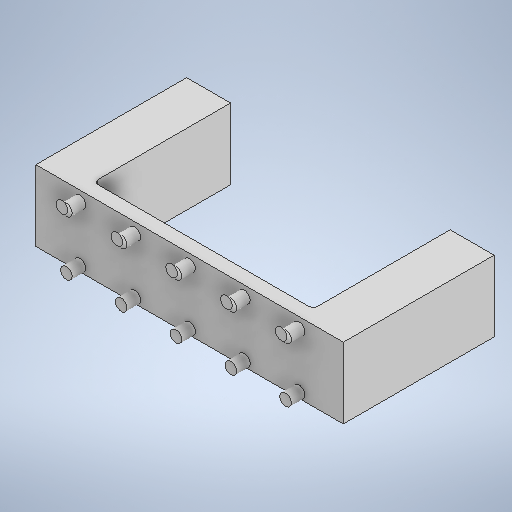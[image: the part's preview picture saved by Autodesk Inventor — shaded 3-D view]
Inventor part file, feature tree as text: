
AUTODESK INVENTOR PART (.ipt)
format: ipt  version: 2025.2 (Build 292293000, 293)  size: 407,552 bytes
history: native  units: mm
features: sketch x6, extrude x5, other x3, pattern_linear x3, fillet x2, delete_face x2, chamfer x2, loft x1, direct_edit x1, projected_geometry x1, move_body x1
ambient origin geometry x8: Origin, YZ Plane, XZ Plane, XY Plane, X Axis, Y Axis, Z Axis, Center Point
bodies: Body1 (feature_tree), Body2 (feature_tree)
feature tree (27):
  other  "Твердое тело1"
  extrude  "Выдавливание1"  Depth=10.0mm
  extrude  "Выдавливание2"  Depth=32.25mm
  pattern_linear  "Прямоуг.массив1"  Spacing1=5.3mm  [1 undecoded]
  extrude  "Выдавливание3"  Depth=6.2mm TaperAngle=0.0deg
  extrude  "Выдавливание4"  Depth=20.0mm
  fillet  "Сопряжение1"  Radius=24.95mm
  pattern_linear  "Прямоуг.массив2"  Spacing1=15.0mm  [1 undecoded]
  fillet  "Сопряжение2"  [1 undecoded]
  other  "РабПлоскость1"
  loft  "Лофт1"
  pattern_linear  "Прямоуг.массив3"  Spacing1=15.0mm  [1 undecoded]
  delete_face  "Delete Face1"
  delete_face  "Delete Face2"
  extrude  "Extrusion6"  TaperAngle=0.0deg  [1 undecoded]
  direct_edit  "Direct Edit1"
  chamfer  "Фаска1"  Distance=60.0mm
  chamfer  "Фаска2"  Distance=2.0mm
  sketch  "Эскиз1"
  sketch  "Эскиз2"
  sketch  "Эскиз3"
  sketch  "Эскиз4"
  sketch  "Эскиз7"
  other  "Ребра1"
  sketch  "Sketch10"  dims[d0=1.85mm d1=0.0mm d2=105.1mm d3=32.25mm d4=5.3mm d13=6.2mm d14=0.0mm d18=20.0mm d20=24.95mm d22=15.0mm d23=0.0mm d27=100.0mm d28=15.0mm d29=0.0mm d31=60.0mm d32=2.0mm d33=10.0mm d35=102.4mm d36=10.0mm d38=62.4mm d39=2.0mm d40=0.15mm d41=64.8mm d42=45.0deg d43=0.15mm d44=64.8mm d45=45.0deg d46=104.8mm d47=66.8mm d51=2.0mm d52=50.0mm d54=24.95mm d55=2.4mm d56=2.4mm d59=2.0mm d60=5.3mm d61=2.0mm d62=0.0mm d63=90.0deg d64=0.0mm d65=90.0deg d67=50.0mm d69=24.95mm d70=20.0mm d71=20.0mm d72=10.0mm d73=0.0mm d74=0.0mm d75=0.0mm d76=17.25mm d50=0.5mm d53=0.872665mm]
  projected_geometry  "Projected Loop4"
  move_body  "Move1"
note: 5 required parameter values undecoded (feature->parameter linkage not recoverable at this tier; creation-order binding heuristic only, values carry confidence <= 0.55)
